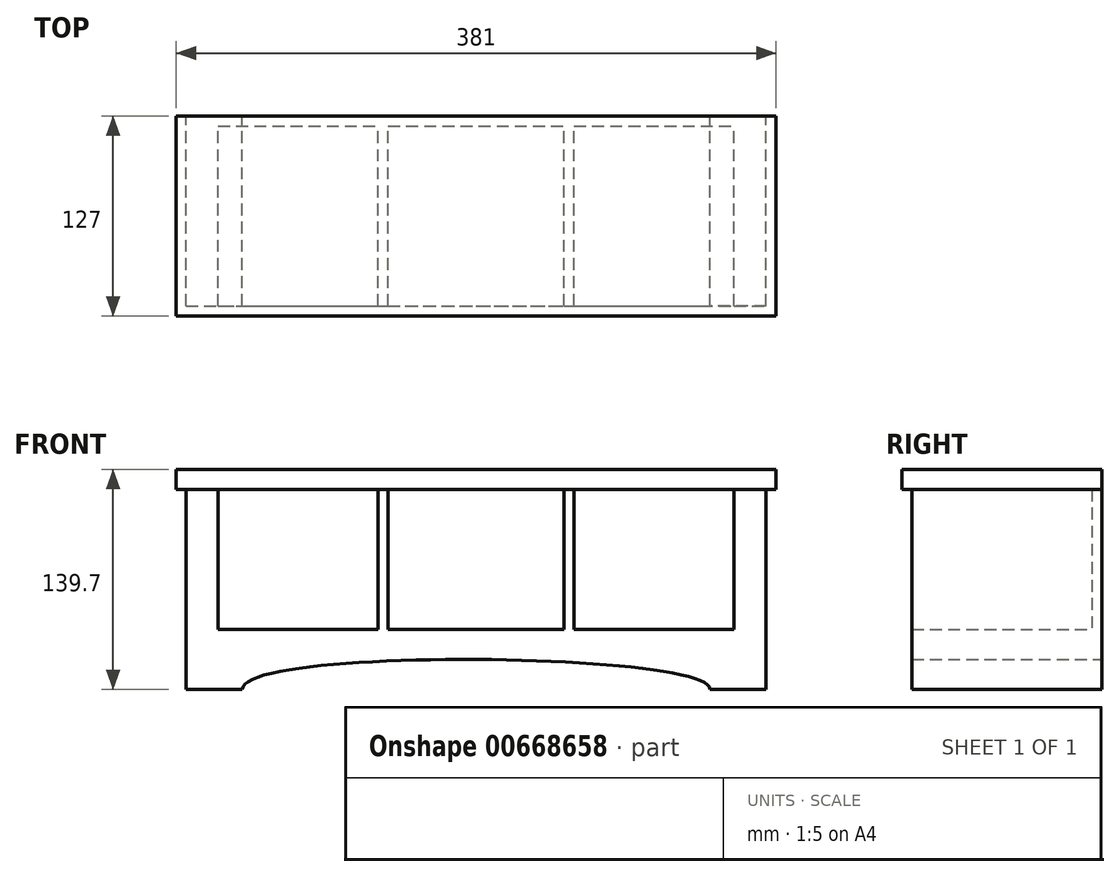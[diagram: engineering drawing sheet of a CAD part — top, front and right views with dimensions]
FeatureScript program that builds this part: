
annotation { "Feature Type Name" : "Feature", "Feature Type Description" : "" }
export const myFeature = defineFeature(function(context is Context, id is Id, definition is map)
    precondition{}
    {
        {
            var Q0;
            Q0=qCreatedBy(makeId("Front.planeOp"),FACE);
            var sketch = newSketch(context, id + "F0", { "sketchPlane" : qUnion([Q0])});
            skLineSegment(sketch, "E0", {"start": v(-190.59, 39.87) * mm, "end": v(190.41, 39.87) * mm});
            skLineSegment(sketch, "E1", {"start": v(-190.59, 39.87) * mm, "end": v(-190.59, 27.17) * mm});
            skLineSegment(sketch, "E2", {"start": v(190.41, 39.87) * mm, "end": v(190.41, 27.17) * mm});
            skLineSegment(sketch, "E3", {"start": v(-190.59, 27.17) * mm, "end": v(-184.24, 27.17) * mm});
            skLineSegment(sketch, "E4", {"start": v(190.41, 27.17) * mm, "end": v(184.06, 27.17) * mm});
            skLineSegment(sketch, "E5", {"start": v(-184.24, 27.17) * mm, "end": v(-184.24, -61.73) * mm});
            skLineSegment(sketch, "E6", {"start": v(184.06, 27.17) * mm, "end": v(184.06, -61.73) * mm});
            skLineSegment(sketch, "E7", {"start": v(-184.24, 27.17) * mm, "end": v(184.06, 27.17) * mm});
            skLineSegment(sketch, "E8", {"start": v(-184.24, -61.73) * mm, "end": v(184.06, -61.73) * mm});
            skLineSegment(sketch, "E9", {"start": v(-184.24, -61.73) * mm, "end": v(-184.24, -99.83) * mm});
            skLineSegment(sketch, "E10", {"start": v(184.06, -61.73) * mm, "end": v(184.06, -99.83) * mm});
            skLineSegment(sketch, "E11", {"start": v(-184.24, -99.83) * mm, "end": v(-148.68, -99.83) * mm});
            skLineSegment(sketch, "E12", {"start": v(184.06, -99.83) * mm, "end": v(148.5, -99.83) * mm});
            skFitSpline(sketch, "E13", {"points": [v(-148.68, -99.83) * mm, v(148.5, -99.83) * mm], "startDerivative": vector(1.16, 81.48) * mm, "endDerivative": vector(0.5, -70.92) * mm});
            skLineSegment(sketch, "E14", {"start": v(-0.09, -61.73) * mm, "end": v(-0.09, -80.78) * mm});
            skLineSegment(sketch, "E15", {"start": v(-163.92, 27.17) * mm, "end": v(-163.92, -61.73) * mm});
            skLineSegment(sketch, "E16", {"start": v(163.74, 27.17) * mm, "end": v(163.74, -61.73) * mm});
            skLineSegment(sketch, "E17", {"start": v(-184.24, -51.58) * mm, "end": v(-163.92, -51.58) * mm});
            skLineSegment(sketch, "E18", {"start": v(163.74, -48.9) * mm, "end": v(184.06, -48.9) * mm});
            skLineSegment(sketch, "E19", {"start": v(-163.92, -26.84) * mm, "end": v(-62.32, -26.84) * mm});
            skLineSegment(sketch, "E20", {"start": v(-62.32, 27.17) * mm, "end": v(-62.32, -61.73) * mm});
            skLineSegment(sketch, "E21", {"start": v(-62.32, -2.91) * mm, "end": v(-55.97, -2.91) * mm});
            skLineSegment(sketch, "E22", {"start": v(-55.97, 27.17) * mm, "end": v(-55.97, -61.73) * mm});
            skLineSegment(sketch, "E23", {"start": v(163.74, -24.73) * mm, "end": v(62.14, -24.73) * mm});
            skLineSegment(sketch, "E24", {"start": v(62.14, 27.17) * mm, "end": v(62.14, -61.73) * mm});
            skLineSegment(sketch, "E25", {"start": v(62.14, -9.95) * mm, "end": v(55.8, -9.95) * mm});
            skLineSegment(sketch, "E26", {"start": v(55.8, 27.17) * mm, "end": v(55.8, -61.73) * mm});
            skLineSegment(sketch, "E27", {"start": v(-55.97, 9.76) * mm, "end": v(55.8, 9.76) * mm});
            skSolve(sketch);
        }
        {
            var Q0;
            Q0=makeQuery(id+"F0.imprint","IMPRINT",FACE,{"disambiguationData":[TD([[makeQuery(id+"F0.imprint","IMPRINT",EDGE,{"derivedFrom":sQuery(id+"F0.wireOp",EDGE,"E0")}),-1.0]])]});
            extrude(context, id + "F1", {"entities" : qUnion([Q0]), "depth" : 127 * mm, "offsetDistance" : 25.4 * mm});
        }
        {
            var Q0;
            {var subQ7=sQuery(id+"F0.wireOp",EDGE,"E9");Q0=makeQuery(id+"F0.imprint","IMPRINT",FACE,{"disambiguationData":[TD([[makeQuery(id+"F0.imprint","IMPRINT",EDGE,{"derivedFrom":subQ7}),1.0]])]});}
            var Q1;
            {var subQ0=sQuery(id+"F0.wireOp",EDGE,"E10");Q1=makeQuery(id+"F0.imprint","IMPRINT",FACE,{"disambiguationData":[TD([[makeQuery(id+"F0.imprint","IMPRINT",EDGE,{"derivedFrom":subQ0}),-1.0]])]});}
            var Q2;
            {var subQ3=sQuery(id+"F0.wireOp",EDGE,"E18");Q2=makeQuery(id+"F0.imprint","IMPRINT",FACE,{"disambiguationData":[TD([[makeQuery(id+"F0.imprint","IMPRINT",EDGE,{"derivedFrom":subQ3}),-1.0]])]});}
            var Q3;
            {var subQ4=sQuery(id+"F0.wireOp",EDGE,"E18");Q3=makeQuery(id+"F0.imprint","IMPRINT",FACE,{"disambiguationData":[TD([[makeQuery(id+"F0.imprint","IMPRINT",EDGE,{"derivedFrom":subQ4}),1.0]])]});}
            var Q4;
            {var subQ4=sQuery(id+"F0.wireOp",EDGE,"E25");Q4=makeQuery(id+"F0.imprint","IMPRINT",FACE,{"disambiguationData":[TD([[makeQuery(id+"F0.imprint","IMPRINT",EDGE,{"derivedFrom":subQ4}),-1.0]])]});}
            var Q5;
            {var subQ4=sQuery(id+"F0.wireOp",EDGE,"E25");Q5=makeQuery(id+"F0.imprint","IMPRINT",FACE,{"disambiguationData":[TD([[makeQuery(id+"F0.imprint","IMPRINT",EDGE,{"derivedFrom":subQ4}),1.0]])]});}
            var Q6;
            {var subQ0=sQuery(id+"F0.wireOp",EDGE,"E17");Q6=makeQuery(id+"F0.imprint","IMPRINT",FACE,{"disambiguationData":[TD([[makeQuery(id+"F0.imprint","IMPRINT",EDGE,{"derivedFrom":subQ0}),1.0]])]});}
            var Q7;
            {var subQ3=sQuery(id+"F0.wireOp",EDGE,"E17");Q7=makeQuery(id+"F0.imprint","IMPRINT",FACE,{"disambiguationData":[TD([[makeQuery(id+"F0.imprint","IMPRINT",EDGE,{"derivedFrom":subQ3}),-1.0]])]});}
            var Q8;
            {var subQ6=sQuery(id+"F0.wireOp",EDGE,"E21");Q8=makeQuery(id+"F0.imprint","IMPRINT",FACE,{"disambiguationData":[TD([[makeQuery(id+"F0.imprint","IMPRINT",EDGE,{"derivedFrom":subQ6}),1.0]])]});}
            var Q9;
            {var subQ4=sQuery(id+"F0.wireOp",EDGE,"E21");Q9=makeQuery(id+"F0.imprint","IMPRINT",FACE,{"disambiguationData":[TD([[makeQuery(id+"F0.imprint","IMPRINT",EDGE,{"derivedFrom":subQ4}),-1.0]])]});}
            extrude(context, id + "F2", {"entities" : qUnion([Q0, Q1, Q2, Q3, Q4, Q5, Q6, Q7, Q8, Q9]), "operationType" : NewBodyOperationType.ADD, "depth" : 120.65 * mm, "offsetDistance" : 25.4 * mm});
        }
        {
            var Q0;
            {var subQ0=sQuery(id+"F0.wireOp",EDGE,"E19");Q0=makeQuery(id+"F0.imprint","IMPRINT",FACE,{"disambiguationData":[TD([[makeQuery(id+"F0.imprint","IMPRINT",EDGE,{"derivedFrom":subQ0}),1.0]])]});}
            var Q1;
            {var subQ0=sQuery(id+"F0.wireOp",EDGE,"E19");Q1=makeQuery(id+"F0.imprint","IMPRINT",FACE,{"disambiguationData":[TD([[makeQuery(id+"F0.imprint","IMPRINT",EDGE,{"derivedFrom":subQ0}),-1.0]])]});}
            var Q2;
            {var subQ5=sQuery(id+"F0.wireOp",EDGE,"E27");Q2=makeQuery(id+"F0.imprint","IMPRINT",FACE,{"disambiguationData":[TD([[makeQuery(id+"F0.imprint","IMPRINT",EDGE,{"derivedFrom":subQ5}),1.0]])]});}
            var Q3;
            {var subQ4=sQuery(id+"F0.wireOp",EDGE,"E27");Q3=makeQuery(id+"F0.imprint","IMPRINT",FACE,{"disambiguationData":[TD([[makeQuery(id+"F0.imprint","IMPRINT",EDGE,{"derivedFrom":subQ4}),-1.0]])]});}
            var Q4;
            {var subQ4=sQuery(id+"F0.wireOp",EDGE,"E23");Q4=makeQuery(id+"F0.imprint","IMPRINT",FACE,{"disambiguationData":[TD([[makeQuery(id+"F0.imprint","IMPRINT",EDGE,{"derivedFrom":subQ4}),-1.0]])]});}
            var Q5;
            {var subQ4=sQuery(id+"F0.wireOp",EDGE,"E23");Q5=makeQuery(id+"F0.imprint","IMPRINT",FACE,{"disambiguationData":[TD([[makeQuery(id+"F0.imprint","IMPRINT",EDGE,{"derivedFrom":subQ4}),1.0]])]});}
            extrude(context, id + "F3", {"entities" : qUnion([Q0, Q1, Q2, Q3, Q4, Q5]), "operationType" : NewBodyOperationType.ADD, "depth" : 6.35 * mm, "offsetDistance" : 25.4 * mm});
        }
    });
